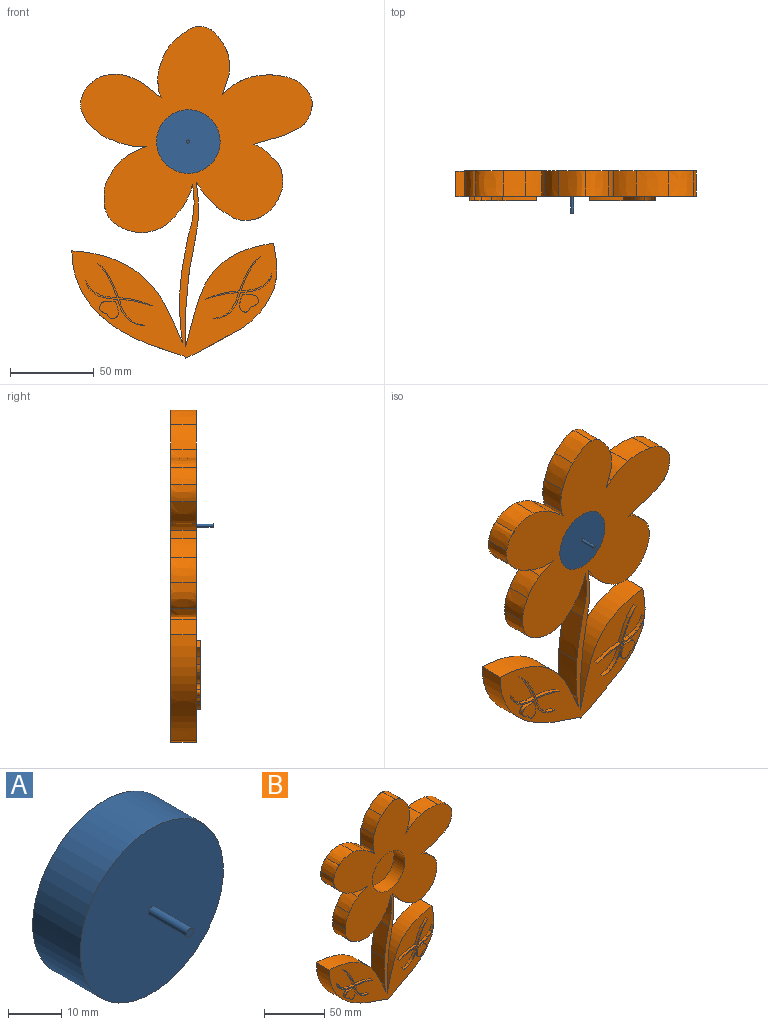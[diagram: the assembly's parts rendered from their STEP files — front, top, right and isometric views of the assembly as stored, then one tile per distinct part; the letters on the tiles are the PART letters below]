
ASSEMBLY  parts=2 mates=1
PART A: 5 faces, bbox 38.1x22.9x38.1 mm
  f0: cylinder r=19.05mm len=38.1mm, axis (0,-1,0), area 1520.1mm2, adj f1,f2
  f1: plane 38.1x38.1mm, normal (0,1,0), area 1140.1mm2, adj f0
  f2: plane 38.1x38.1mm, normal (0,-1,0), area 1137.2mm2, adj f0,f3
  f3: cylinder r=0.95mm len=10.16mm, axis (0,1,0), area 60.8mm2, adj f2,f4
  f4: plane 1.91x1.91mm, normal (0,-1,0), area 2.9mm2, adj f3
PART B: 103 faces, bbox 145x17.8x199.5 mm
  f0: plane 199.55x144.97mm, normal (0,-1,0), area 13239.2mm2, adj f1,f2,f3,f4,f5,f6,f7,f8
  f1: extruded ~29.92x15.24mm, area 458.3mm2, adj f0,f2,f49,f50
  f2: extruded ~18.79x18.53mm, area 407.1mm2, adj f0,f1,f3,f50
  f3: extruded ~19.59x15.24mm, area 318.1mm2, adj f0,f2,f4,f50
  f4: extruded ~16.81x15.24mm, area 336.5mm2, adj f0,f3,f5,f50
  f5: extruded ~17.03x15.24mm, area 278.3mm2, adj f0,f4,f6,f50
  f6: extruded ~15.24x13.04mm, area 250.7mm2, adj f0,f5,f7,f50
  f7: extruded ~29.98x15.24mm, area 495.8mm2, adj f0,f6,f8,f50
  f8: extruded ~18.46x15.24mm, area 308.5mm2, adj f0,f7,f9,f50
  f9: extruded ~15.24x14.52mm, area 278.8mm2, adj f0,f8,f10,f50
  f10: extruded ~19.55x15.24mm, area 300.2mm2, adj f0,f9,f11,f50
  f11: extruded ~15.24x13.64mm, area 234.4mm2, adj f0,f10,f12,f50
  f12: plane 15.24x4.27mm, normal (-0.65,0,0.76), area 86.1mm2, adj f0,f11,f13,f50
  f13: plane 15.24x12.67mm, normal (0.95,0,-0.32), area 203.8mm2, adj f0,f12,f14,f50
  f14: extruded ~16.19x15.24mm, area 254mm2, adj f0,f13,f15,f50
  f15: extruded ~15.24x13.74mm, area 286.3mm2, adj f0,f14,f16,f50
  f16: extruded ~16.16x15.24mm, area 287.3mm2, adj f0,f15,f17,f50
  f17: extruded ~15.24x15.04mm, area 268.9mm2, adj f0,f16,f18,f50
  f18: extruded ~15.59x15.24mm, area 240.7mm2, adj f0,f17,f19,f50
  f19: extruded ~15.24x3.64mm, area 58.9mm2, adj f0,f18,f20,f50
  f20: extruded ~15.24x11.85mm, area 228mm2, adj f0,f19,f21,f50
  f21: extruded ~15.24x12.72mm, area 208.7mm2, adj f0,f20,f22,f50
  f22: extruded ~16.91x15.24mm, area 281.8mm2, adj f0,f21,f23,f50
  f23: extruded ~15.24x10.46mm, area 194.4mm2, adj f0,f22,f24,f50
  f24: extruded ~15.24x10.3mm, area 164mm2, adj f0,f23,f25,f50
  f25: extruded ~16.7x15.24mm, area 330.5mm2, adj f0,f24,f26,f50
  f26: extruded ~15.24x12.19mm, area 195mm2, adj f0,f25,f27,f50
  f27: plane 15.24x8.53mm, normal (0,0,-1), area 130mm2, adj f0,f26,f28,f50
  f28: extruded ~15.24x11.11mm, area 187.3mm2, adj f0,f27,f29,f50
  f29: extruded ~15.24x11.25mm, area 235.9mm2, adj f0,f28,f30,f50
  f30: extruded ~15.24x14.82mm, area 239.9mm2, adj f0,f29,f31,f50
  f31: extruded ~15.84x15.24mm, area 284.5mm2, adj f0,f30,f32,f50
  f32: extruded ~20.63x15.24mm, area 329.9mm2, adj f0,f31,f33,f50
  f33: extruded ~15.92x15.24mm, area 303.5mm2, adj f0,f32,f34,f50
  f34: extruded ~16.77x15.24mm, area 293.4mm2, adj f0,f33,f35,f50
  f35: extruded ~30.35x15.24mm, area 469.3mm2, adj f0,f34,f36,f50
  f36: extruded ~29.85x15.24mm, area 461mm2, adj f0,f35,f37,f50
  f37: extruded ~26.05x15.24mm, area 397.4mm2, adj f0,f36,f38,f50
  f38: extruded ~15.24x8.01mm, area 124mm2, adj f0,f37,f39,f50
  f39: extruded ~66.21x54.72mm, area 1409.6mm2, adj f0,f38,f40,f50
  f40: extruded ~68.15x64.15mm, area 1544.5mm2, adj f0,f39,f41,f50
  f41: plane 15.24x8.32mm, normal (0.42,0,-0.91), area 139.4mm2, adj f0,f40,f42,f50
  f42: extruded ~26.78x15.24mm, area 467.3mm2, adj f0,f41,f43,f50
  f43: extruded ~21.55x17.59mm, area 428.4mm2, adj f0,f42,f44,f50
  f44: extruded ~28.52x15.24mm, area 440mm2, adj f0,f43,f45,f50
  f45: extruded ~62.17x52.69mm, area 1360.4mm2, adj f0,f44,f46,f50
  f46: plane 17.03x15.24mm, normal (1,0,0), area 259.6mm2, adj f0,f45,f47,f50
  f47: extruded ~16.25x15.24mm, area 248.4mm2, adj f0,f46,f48,f50
  f48: extruded ~24.52x15.24mm, area 377.8mm2, adj f0,f47,f49,f50
  f49: extruded ~15.24x10.72mm, area 165.9mm2, adj f0,f1,f48,f50
  f50: plane 199.55x144.97mm, normal (0,1,0), area 14693.2mm2, adj f1,f2,f3,f4,f5,f6,f7,f8
  f51: extruded ~5.82x2.54mm, area 14.9mm2, adj f0,f52,f69,f70
  f52: extruded ~6.05x2.54mm, area 16.2mm2, adj f0,f51,f53,f70
  f53: extruded ~4.05x3.15mm, area 13.1mm2, adj f0,f52,f54,f70
  f54: extruded ~4.56x2.58mm, area 13.4mm2, adj f0,f53,f55,f70
  f55: extruded ~4.64x2.54mm, area 12.7mm2, adj f0,f54,f56,f70
  f56: extruded ~15.18x6.51mm, area 43.4mm2, adj f0,f55,f57,f70
  f57: plane 2.54x1.87mm, normal (0,0,-1), area 4.8mm2, adj f0,f56,f58,f70
  f58: extruded ~12.36x6.44mm, area 35.9mm2, adj f0,f57,f59,f70
  f59: extruded ~9.61x3.34mm, area 26.4mm2, adj f0,f58,f60,f70
  f60: extruded ~6.31x2.54mm, area 16.8mm2, adj f0,f59,f61,f70
  f61: extruded ~5.14x5.1mm, area 18.6mm2, adj f0,f60,f62,f70
  f62: extruded ~8.6x3.34mm, area 23.6mm2, adj f0,f61,f63,f70
  f63: extruded ~19.65x4.05mm, area 51.1mm2, adj f0,f62,f64,f70
  f64: extruded ~20.09x5.06mm, area 52.9mm2, adj f0,f63,f65,f70
  f65: extruded ~14.55x6.85mm, area 40.9mm2, adj f0,f64,f66,f70
  f66: extruded ~5.91x5.9mm, area 21.4mm2, adj f0,f65,f67,f70
  f67: extruded ~5.58x4.88mm, area 18.9mm2, adj f0,f66,f68,f70
  f68: plane 7.54x3.99mm, normal (-0.88,0,-0.47), area 21.7mm2, adj f0,f67,f69,f70
  f69: plane 7.27x2.74mm, normal (-0.94,0,-0.35), area 19.7mm2, adj f0,f51,f68,f70
  f70: plane 39.74x37.52mm, normal (0,-1,0), area 70.2mm2, adj f51,f52,f53,f54,f55,f56,f57,f58
  f71: extruded ~7.44x2.54mm, area 19.6mm2, adj f0,f72,f74,f75
  f72: extruded ~9.14x2.62mm, area 25.9mm2, adj f0,f71,f73,f75
  f73: extruded ~4.77x4.4mm, area 18.9mm2, adj f0,f72,f74,f75
  f74: extruded ~6.89x3.25mm, area 25.4mm2, adj f0,f71,f73,f75
  f75: plane 12.36x12.14mm, normal (0,-1,0), area 86.7mm2, adj f71,f72,f73,f74
  f76: extruded ~7.44x2.54mm, area 19.6mm2, adj f0,f77,f79,f80
  f77: extruded ~6.89x3.25mm, area 25.4mm2, adj f0,f76,f78,f80
  f78: extruded ~4.77x4.4mm, area 18.9mm2, adj f0,f77,f79,f80
  f79: extruded ~9.14x2.62mm, area 25.9mm2, adj f0,f76,f78,f80
  f80: plane 12.36x12.14mm, normal (0,-1,0), area 86.7mm2, adj f76,f77,f78,f79
  f81: extruded ~5.14x5.1mm, area 18.6mm2, adj f0,f82,f99,f100
  f82: extruded ~6.31x2.54mm, area 16.8mm2, adj f0,f81,f83,f100
  f83: extruded ~9.61x3.34mm, area 26.4mm2, adj f0,f82,f84,f100
  f84: extruded ~12.36x6.44mm, area 35.9mm2, adj f0,f83,f85,f100
  f85: plane 2.54x1.87mm, normal (0,0,-1), area 4.8mm2, adj f0,f84,f86,f100
  f86: extruded ~15.18x6.51mm, area 43.4mm2, adj f0,f85,f87,f100
  f87: extruded ~4.64x2.54mm, area 12.7mm2, adj f0,f86,f88,f100
  f88: extruded ~4.56x2.58mm, area 13.4mm2, adj f0,f87,f89,f100
  f89: extruded ~4.05x3.15mm, area 13.1mm2, adj f0,f88,f90,f100
  f90: extruded ~6.05x2.54mm, area 16.2mm2, adj f0,f89,f91,f100
  f91: extruded ~5.82x2.54mm, area 14.9mm2, adj f0,f90,f92,f100
  f92: plane 7.27x2.74mm, normal (0.94,0,-0.35), area 19.7mm2, adj f0,f91,f93,f100
  f93: plane 7.54x3.99mm, normal (0.88,0,-0.47), area 21.7mm2, adj f0,f92,f94,f100
  f94: extruded ~5.58x4.88mm, area 18.9mm2, adj f0,f93,f95,f100
  f95: extruded ~5.91x5.9mm, area 21.4mm2, adj f0,f94,f96,f100
  f96: extruded ~14.55x6.85mm, area 40.9mm2, adj f0,f95,f97,f100
  f97: extruded ~20.09x5.06mm, area 52.9mm2, adj f0,f96,f98,f100
  f98: extruded ~19.65x4.05mm, area 51.1mm2, adj f0,f97,f99,f100
  f99: extruded ~8.6x3.34mm, area 23.6mm2, adj f0,f81,f98,f100
  f100: plane 39.74x37.52mm, normal (0,-1,0), area 70.2mm2, adj f81,f82,f83,f84,f85,f86,f87,f88
  f101: cylinder r=19.05mm len=38.1mm, axis (0,-1,0), area 1520.1mm2, adj f0,f102
  f102: plane 38.1x38.1mm, normal (0,-1,0), area 1140.1mm2, adj f101
PLACE A t=(-117.5,-34.05,62.72)mm
PLACE B t=(-117.5,-18.81,62.72)mm
MATE fastened B.f101 <-> A.f0  axis (0,-1,0) through (-117.5,-21.35,62.72)mm
